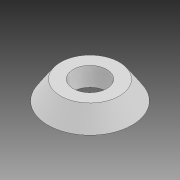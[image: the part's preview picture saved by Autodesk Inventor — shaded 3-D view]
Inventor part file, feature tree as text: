
AUTODESK INVENTOR PART (.ipt)
format: ipt  version: 2020 (Build 240168000, 168)  size: 88,576 bytes
history: native  units: mm
features: revolve x1, sketch x1
ambient origin geometry x8: Origin, YZ Plane, XZ Plane, XY Plane, X Axis, Y Axis, Z Axis, Center Point
bodies: Solid1 (feature_tree)
feature tree (2):
  revolve  "Revolution1"  [1 undecoded]
  sketch  "Sketch1"  dims[d0=2.65mm d1=3.0mm d2=2.0mm d3=4.0mm d4=90.0deg]
note: 1 required parameter value undecoded (feature->parameter linkage not recoverable at this tier; creation-order binding heuristic only, values carry confidence <= 0.55)
